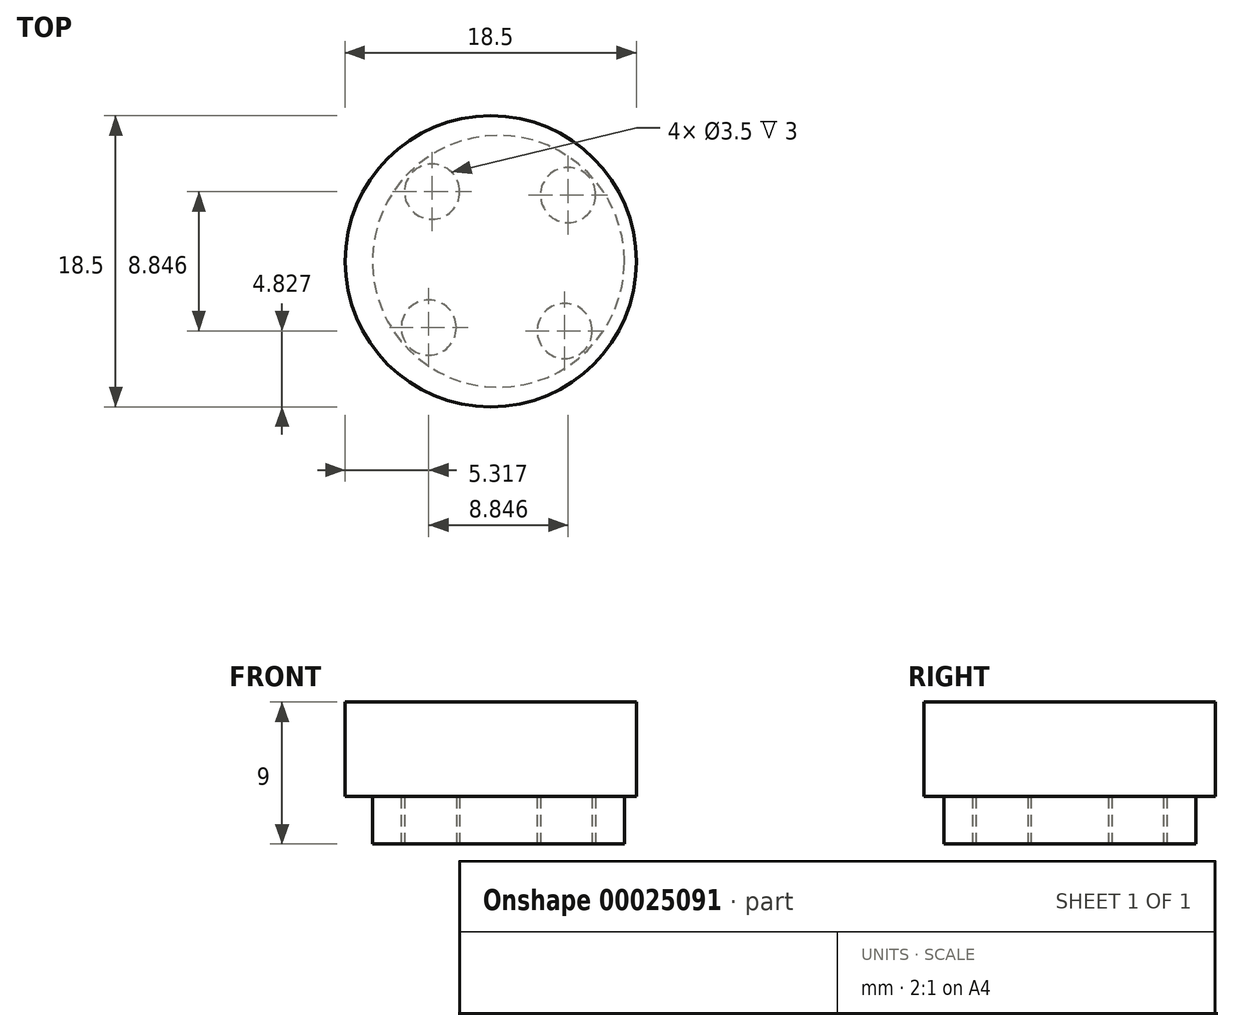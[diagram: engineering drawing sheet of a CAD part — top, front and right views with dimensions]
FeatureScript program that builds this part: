
annotation { "Feature Type Name" : "Feature", "Feature Type Description" : "" }
export const myFeature = defineFeature(function(context is Context, id is Id, definition is map)
    precondition{}
    {
        {
            var Q0;
            Q0=qCreatedBy(makeId("Top.planeOp"),FACE);
            var sketch = newSketch(context, id + "F0", { "sketchPlane" : qUnion([Q0])});
            skCircle(sketch, "E0", {"center": v(0, 0) * mm, "radius": 8 * mm});
            skCircle(sketch, "E1", {"center": v(0, 0) * mm, "radius": 4 * mm});
            skCircle(sketch, "E2", {"center": v(0, 0) * mm, "radius": 1.75 * mm});
            skCircle(sketch, "E3", {"center": v(-4.21, 4.42) * mm, "radius": 1.75 * mm});
            skCircle(sketch, "E4.1.0", {"center": v(-4.42, -4.21) * mm, "radius": 1.75 * mm});
            skCircle(sketch, "E4.2.0", {"center": v(4.21, -4.42) * mm, "radius": 1.75 * mm});
            skCircle(sketch, "E4.3.0", {"center": v(4.42, 4.21) * mm, "radius": 1.75 * mm});
            skSolve(sketch);
        }
        {
            var Q0;
            Q0 = qSketchRegion(id + "F0", true);
            var Q1;
            Q1=makeQuery(id+"F0.imprint","IMPRINT",FACE,{"disambiguationData":[TD([[makeQuery(id+"F0.imprint","IMPRINT",EDGE,{"derivedFrom":sQuery(id+"F0.wireOp",EDGE,"E1")}),1.0]])]});
            var Q2;
            Q2=makeQuery(id+"F0.imprint","IMPRINT",FACE,{"disambiguationData":[TD([[makeQuery(id+"F0.imprint","IMPRINT",EDGE,{"derivedFrom":sQuery(id+"F0.wireOp",EDGE,"E2")}),1.0]])]});
            extrude(context, id + "F1", {"entities" : qUnion([Q0, Q1, Q2]), "depth" : 3 * mm});
        }
        {
            var Q0;
            Q0=makeQuery(id+"F1.opExtrude","CAP_FACE",FACE,{"disambiguationData":[OSD([sQuery(id+"F0.wireOp",EDGE,"E0"),sQuery(id+"F0.wireOp",EDGE,"E3"),sQuery(id+"F0.wireOp",EDGE,"E4.1.0"),sQuery(id+"F0.wireOp",EDGE,"E4.2.0"),sQuery(id+"F0.wireOp",EDGE,"E4.3.0")])],"isStart":false});
            var sketch = newSketch(context, id + "F2", { "sketchPlane" : qUnion([Q0])});
            skCircle(sketch, "E5", {"center": v(-0.49, 0) * mm, "radius": 9.25 * mm});
            skSolve(sketch);
        }
        {
            var Q0;
            Q0 = qSketchRegion(id + "F2", true);
            extrude(context, id + "F3", {"entities" : qUnion([Q0]), "operationType" : NewBodyOperationType.ADD, "depth" : 6 * mm});
        }
    });
